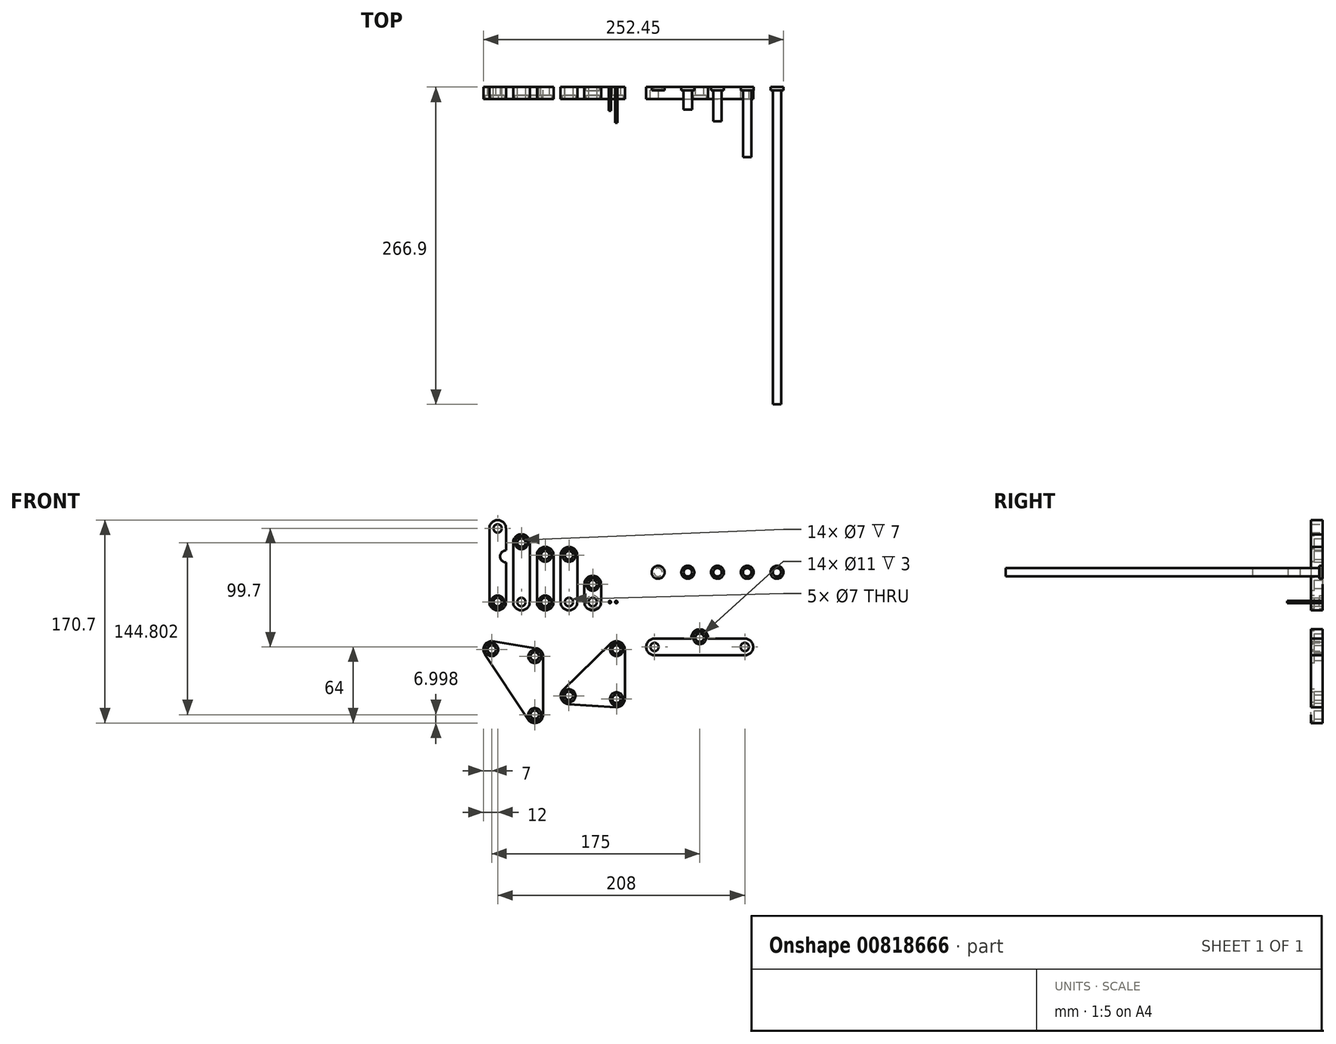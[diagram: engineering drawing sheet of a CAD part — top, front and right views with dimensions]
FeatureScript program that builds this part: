
annotation { "Feature Type Name" : "Feature", "Feature Type Description" : "" }
export const myFeature = defineFeature(function(context is Context, id is Id, definition is map)
    precondition{}
    {
        {
            assignVariable(context, id + "F0", {"name" : "thinkress", "anyValue" : 10});
        }
        {
            var Q0;
            Q0=qCreatedBy(makeId("Front.planeOp"),FACE);
            var sketch = newSketch(context, id + "F1", { "sketchPlane" : qUnion([Q0])});
            skArc(sketch, "E0", {"start": v(-3, 15) * mm, "mid": v(-10, 22) * mm, "end": v(-17, 15) * mm});
            skLineSegment(sketch, "E1", {"start": v(-17, 15) * mm, "end": v(-17, 0) * mm});
            skLineSegment(sketch, "E2", {"start": v(-3, 15) * mm, "end": v(-3, 0) * mm});
            skCircle(sketch, "E3", {"center": v(-10, 15) * mm, "radius": 3.5 * mm});
            skCircle(sketch, "E4", {"center": v(-10, 0) * mm, "radius": 3.5 * mm});
            skArc(sketch, "E5", {"start": v(-37, 0) * mm, "mid": v(-30, -7) * mm, "end": v(-23, 0) * mm});
            skArc(sketch, "E6", {"start": v(-23, 39.3) * mm, "mid": v(-30, 46.3) * mm, "end": v(-37, 39.3) * mm});
            skLineSegment(sketch, "E7", {"start": v(-37, 39.3) * mm, "end": v(-37, 0) * mm});
            skLineSegment(sketch, "E8", {"start": v(-23, 39.3) * mm, "end": v(-23, 0) * mm});
            skCircle(sketch, "E9", {"center": v(-30, 39.3) * mm, "radius": 3.5 * mm});
            skCircle(sketch, "E10", {"center": v(-30, 0) * mm, "radius": 3.5 * mm});
            skArc(sketch, "E11", {"start": v(-57, 0) * mm, "mid": v(-50, -7) * mm, "end": v(-43, 0) * mm});
            skArc(sketch, "E12", {"start": v(-43, 39.4) * mm, "mid": v(-50, 46.4) * mm, "end": v(-57, 39.4) * mm});
            skLineSegment(sketch, "E13", {"start": v(-57, 39.4) * mm, "end": v(-57, 0) * mm});
            skLineSegment(sketch, "E14", {"start": v(-43, 39.4) * mm, "end": v(-43, 0) * mm});
            skCircle(sketch, "E15", {"center": v(-50, 39.4) * mm, "radius": 3.5 * mm});
            skCircle(sketch, "E16", {"center": v(-50, 0) * mm, "radius": 3.5 * mm});
            skArc(sketch, "E17", {"start": v(-77, 0) * mm, "mid": v(-70, -7) * mm, "end": v(-63, 0) * mm});
            skArc(sketch, "E18", {"start": v(-63, 50) * mm, "mid": v(-70, 57) * mm, "end": v(-77, 50) * mm});
            skLineSegment(sketch, "E19", {"start": v(-77, 50) * mm, "end": v(-77, 0) * mm});
            skLineSegment(sketch, "E20", {"start": v(-63, 50) * mm, "end": v(-63, 0) * mm});
            skCircle(sketch, "E21", {"center": v(-70, 50) * mm, "radius": 3.5 * mm});
            skCircle(sketch, "E22", {"center": v(-70, 0) * mm, "radius": 3.5 * mm});
            skArc(sketch, "E23", {"start": v(-97, 0) * mm, "mid": v(-90, -7) * mm, "end": v(-83, 0) * mm});
            skArc(sketch, "E24", {"start": v(-83, 61.9) * mm, "mid": v(-90, 68.9) * mm, "end": v(-97, 61.9) * mm});
            skLineSegment(sketch, "E25", {"start": v(-97, 61.9) * mm, "end": v(-97, 0) * mm});
            skLineSegment(sketch, "E26", {"start": v(-83, 61.9) * mm, "end": v(-83, 0) * mm});
            skCircle(sketch, "E27", {"center": v(-90, 61.9) * mm, "radius": 3.5 * mm});
            skCircle(sketch, "E28", {"center": v(-90, 0) * mm, "radius": 3.5 * mm});
            skLineSegment(sketch, "E29", {"start": v(10, -81.5) * mm, "end": v(10, -40) * mm, "construction": true});
            skLineSegment(sketch, "E30", {"start": v(10, -40) * mm, "end": v(-30.01, -78.9) * mm, "construction": true});
            skLineSegment(sketch, "E31", {"start": v(-30.01, -78.9) * mm, "end": v(10, -81.5) * mm, "construction": true});
            skLineSegment(sketch, "E32", {"start": v(-95, -40) * mm, "end": v(-58.76, -45.8) * mm, "construction": true});
            skPoint(sketch, "E32.startSnap0", {"position": v(-50, -7) * mm});
            skLineSegment(sketch, "E33", {"start": v(-58.76, -45.8) * mm, "end": v(-58.76, -94.8) * mm, "construction": true});
            skLineSegment(sketch, "E34", {"start": v(-58.76, -94.8) * mm, "end": v(-95, -40) * mm, "construction": true});
            skArc(sketch, "E35", {"start": v(17, -40) * mm, "mid": v(12.72, -33.55) * mm, "end": v(5.12, -34.98) * mm});
            skArc(sketch, "E36", {"start": v(9.54, -88.49) * mm, "mid": v(14.79, -86.6) * mm, "end": v(17, -81.5) * mm});
            skArc(sketch, "E37", {"start": v(-34.9, -73.87) * mm, "mid": v(-36.58, -81.31) * mm, "end": v(-30.47, -85.88) * mm});
            skLineSegment(sketch, "E38.0", {"start": v(5.12, -34.98) * mm, "end": v(-34.9, -73.87) * mm});
            skLineSegment(sketch, "E39.0", {"start": v(17, -81.5) * mm, "end": v(17, -40) * mm});
            skLineSegment(sketch, "E40.0", {"start": v(-30.47, -85.88) * mm, "end": v(9.54, -88.49) * mm});
            skCircle(sketch, "E41", {"center": v(-30.01, -78.9) * mm, "radius": 3.5 * mm});
            skCircle(sketch, "E42", {"center": v(10, -40) * mm, "radius": 3.5 * mm});
            skCircle(sketch, "E43", {"center": v(10, -81.5) * mm, "radius": 3.5 * mm});
            skArc(sketch, "E44", {"start": v(-93.9, -33.09) * mm, "mid": v(-100.88, -36.2) * mm, "end": v(-100.84, -43.86) * mm});
            skArc(sketch, "E45", {"start": v(-64.6, -98.66) * mm, "mid": v(-56.75, -101.5) * mm, "end": v(-51.76, -94.8) * mm});
            skArc(sketch, "E46", {"start": v(-51.76, -45.8) * mm, "mid": v(-53.43, -41.26) * mm, "end": v(-57.65, -38.9) * mm});
            skLineSegment(sketch, "E47.0", {"start": v(-64.6, -98.66) * mm, "end": v(-100.84, -43.86) * mm});
            skLineSegment(sketch, "E48.0", {"start": v(-93.9, -33.09) * mm, "end": v(-57.65, -38.9) * mm});
            skLineSegment(sketch, "E49.0", {"start": v(-51.76, -45.8) * mm, "end": v(-51.76, -94.8) * mm});
            skCircle(sketch, "E50", {"center": v(-95, -40) * mm, "radius": 3.5 * mm});
            skCircle(sketch, "E51", {"center": v(-58.76, -45.8) * mm, "radius": 3.5 * mm});
            skCircle(sketch, "E52", {"center": v(-58.76, -94.8) * mm, "radius": 3.5 * mm});
            skLineSegment(sketch, "E53", {"start": v(42, -37.8) * mm, "end": v(80, -37.8) * mm, "construction": true});
            skLineSegment(sketch, "E54", {"start": v(80, -37.8) * mm, "end": v(118, -37.8) * mm, "construction": true});
            skLineSegment(sketch, "E55", {"start": v(80, -37.8) * mm, "end": v(80, -30) * mm, "construction": true});
            skArc(sketch, "E56", {"start": v(42, -30.8) * mm, "mid": v(35, -37.8) * mm, "end": v(42, -44.8) * mm});
            skArc(sketch, "E57", {"start": v(118, -44.8) * mm, "mid": v(125, -37.8) * mm, "end": v(118, -30.8) * mm});
            skArc(sketch, "E58", {"start": v(87, -30) * mm, "mid": v(80, -23) * mm, "end": v(73, -30) * mm});
            skLineSegment(sketch, "E59", {"start": v(42, -44.8) * mm, "end": v(118, -44.8) * mm});
            skLineSegment(sketch, "E60", {"start": v(42, -30.8) * mm, "end": v(73, -30.8) * mm});
            skLineSegment(sketch, "E61", {"start": v(73, -30) * mm, "end": v(73, -30.8) * mm});
            skLineSegment(sketch, "E62", {"start": v(118, -30.8) * mm, "end": v(87, -30.8) * mm});
            skLineSegment(sketch, "E63", {"start": v(87, -30) * mm, "end": v(87, -30.8) * mm});
            skCircle(sketch, "E64", {"center": v(80, -30) * mm, "radius": 3.5 * mm});
            skCircle(sketch, "E65", {"center": v(118, -37.8) * mm, "radius": 3.5 * mm});
            skCircle(sketch, "E66", {"center": v(42, -37.8) * mm, "radius": 3.5 * mm});
            skArc(sketch, "E67", {"start": v(-17, 0) * mm, "mid": v(-10, -7) * mm, "end": v(-3, 0) * mm});
            skSolve(sketch);
        }
        {
            var Q0;
            Q0=makeQuery(id+"F1.imprint","IMPRINT",FACE,{"disambiguationData":[TD([[makeQuery(id+"F1.imprint","IMPRINT",EDGE,{"derivedFrom":sQuery(id+"F1.wireOp",EDGE,"E35")}),1.0]])]});
            var Q1;
            Q1=makeQuery(id+"F1.imprint","IMPRINT",FACE,{"disambiguationData":[TD([[makeQuery(id+"F1.imprint","IMPRINT",EDGE,{"derivedFrom":sQuery(id+"F1.wireOp",EDGE,"E44")}),1.0]])]});
            var Q2;
            Q2=makeQuery(id+"F1.imprint","IMPRINT",FACE,{"disambiguationData":[TD([[makeQuery(id+"F1.imprint","IMPRINT",EDGE,{"derivedFrom":sQuery(id+"F1.wireOp",EDGE,"E23")}),1.0]])]});
            var Q3;
            Q3=makeQuery(id+"F1.imprint","IMPRINT",FACE,{"disambiguationData":[TD([[makeQuery(id+"F1.imprint","IMPRINT",EDGE,{"derivedFrom":sQuery(id+"F1.wireOp",EDGE,"E17")}),1.0]])]});
            var Q4;
            Q4=makeQuery(id+"F1.imprint","IMPRINT",FACE,{"disambiguationData":[TD([[makeQuery(id+"F1.imprint","IMPRINT",EDGE,{"derivedFrom":sQuery(id+"F1.wireOp",EDGE,"E11")}),1.0]])]});
            var Q5;
            Q5=makeQuery(id+"F1.imprint","IMPRINT",FACE,{"disambiguationData":[TD([[makeQuery(id+"F1.imprint","IMPRINT",EDGE,{"derivedFrom":sQuery(id+"F1.wireOp",EDGE,"E5")}),1.0]])]});
            var Q6;
            Q6=makeQuery(id+"F1.imprint","IMPRINT",FACE,{"disambiguationData":[TD([[makeQuery(id+"F1.imprint","IMPRINT",EDGE,{"derivedFrom":sQuery(id+"F1.wireOp",EDGE,"EmJazmCR-fPvo-Zdi6-Hvz8-qesBlYHY8SAY")}),1.0]])]});
            var Q7;
            Q7=makeQuery(id+"F1.imprint","IMPRINT",FACE,{"disambiguationData":[TD([[makeQuery(id+"F1.imprint","IMPRINT",EDGE,{"derivedFrom":sQuery(id+"F1.wireOp",EDGE,"E56")}),1.0]])]});
            var Q8;
            Q8=makeQuery(id+"F1.imprint","IMPRINT",FACE,{"disambiguationData":[TD([[makeQuery(id+"F1.imprint","IMPRINT",EDGE,{"derivedFrom":sQuery(id+"F1.wireOp",EDGE,"E0")}),1.0]])]});
            extrude(context, id + "F2", {"entities" : qUnion([Q0, Q1, Q2, Q3, Q4, Q5, Q6, Q7, Q8]), "depth" : (getVariable(context, 'thinkress')) * mm, "offsetDistance" : 25 * mm});
        }
        {
            var Q0;
            Q0=qCreatedBy(makeId("Front.planeOp"),FACE);
            var sketch = newSketch(context, id + "F3", { "sketchPlane" : qUnion([Q0])});
            skCircle(sketch, "E68", {"center": v(4.4, 0) * mm, "radius": 1 * mm});
            skCircle(sketch, "E69", {"center": v(9.8, 0) * mm, "radius": 1 * mm});
            skSolve(sketch);
        }
        {
            var Q0;
            Q0=makeQuery(id+"F3.imprint","IMPRINT",FACE,{"disambiguationData":[TD([[makeQuery(id+"F3.imprint","IMPRINT",EDGE,{"derivedFrom":sQuery(id+"F3.wireOp",EDGE,"E68")}),1.0]])]});
            extrude(context, id + "F4", {"entities" : qUnion([Q0]), "depth" : (getVariable(context, 'thinkress') * 2) * mm, "offsetDistance" : 25 * mm});
        }
        {
            var Q0;
            Q0=makeQuery(id+"F3.imprint","IMPRINT",FACE,{"disambiguationData":[TD([[makeQuery(id+"F3.imprint","IMPRINT",EDGE,{"derivedFrom":sQuery(id+"F3.wireOp",EDGE,"E69")}),1.0]])]});
            extrude(context, id + "F5", {"entities" : qUnion([Q0]), "depth" : (getVariable(context, 'thinkress') * 3) * mm, "offsetDistance" : 25 * mm});
        }
        {
            var Q0;
            Q0=makeQuery(id+"F2.opExtrude","CAP_FACE",FACE,{"disambiguationData":[OSD([sQuery(id+"F1.wireOp",EDGE,"E23"),sQuery(id+"F1.wireOp",EDGE,"E24"),sQuery(id+"F1.wireOp",EDGE,"E25"),sQuery(id+"F1.wireOp",EDGE,"E26"),sQuery(id+"F1.wireOp",EDGE,"E27"),sQuery(id+"F1.wireOp",EDGE,"E28")])],"isStart":false});
            var sketch = newSketch(context, id + "F6", { "sketchPlane" : qUnion([Q0])});
            skArc(sketch, "E70", {"start": v(-83, 43.4) * mm, "mid": v(-88, 38.4) * mm, "end": v(-83, 33.4) * mm});
            skLineSegment(sketch, "E71.0", {"start": v(-83, 43.4) * mm, "end": v(-83, 33.4) * mm});
            skPoint(sketch, "E72.orphan", {"position": v(-83, 61.9) * mm});
            skPoint(sketch, "E73.orphan", {"position": v(-83, 0) * mm});
            skSolve(sketch);
        }
        {
            var Q0;
            Q0 = qSketchRegion(id + "F6", true);
            extrude(context, id + "F7", {"entities" : qUnion([Q0]), "operationType" : NewBodyOperationType.REMOVE, "endBound" : BoundingType.UP_TO_NEXT, "oppositeDirection" : true, "depth" : 25 * mm, "offsetDistance" : 25 * mm});
        }
        {
            assignVariable(context, id + "F8", {"name" : "nailRoundHigh", "anyValue" : 3});
        }
        {
            assignVariable(context, id + "F9", {"name" : "boardLength", "anyValue" : 110});
        }
        {
            var Q0;
            Q0=makeQuery(id+"F2.opExtrude","CAP_FACE",FACE,{"disambiguationData":[OSD([sQuery(id+"F1.wireOp",EDGE,"E0"),sQuery(id+"F1.wireOp",EDGE,"E1"),sQuery(id+"F1.wireOp",EDGE,"E2"),sQuery(id+"F1.wireOp",EDGE,"E3"),sQuery(id+"F1.wireOp",EDGE,"E4"),sQuery(id+"F1.wireOp",EDGE,"E67")])],"isStart":false});
            var sketch = newSketch(context, id + "F10", { "sketchPlane" : qUnion([Q0])});
            skCircle(sketch, "E74", {"center": v(-10, 15) * mm, "radius": 5.5 * mm});
            skCircle(sketch, "E75", {"center": v(-10, 0) * mm, "radius": 5.5 * mm});
            skSolve(sketch);
        }
        {
            var Q0;
            Q0=makeQuery(id+"F10.imprint","IMPRINT",FACE,{"disambiguationData":[TD([[makeQuery(id+"F10.imprint","IMPRINT",EDGE,{"derivedFrom":sQuery(id+"F10.wireOp",EDGE,"E74")}),1.0]])]});
            extrude(context, id + "F11", {"entities" : qUnion([Q0]), "operationType" : NewBodyOperationType.REMOVE, "oppositeDirection" : true, "depth" : (getVariable(context, 'nailRoundHigh')) * mm, "offsetDistance" : 25 * mm});
        }
        {
            var Q0;
            Q0=makeQuery(id+"F2.opExtrude","CAP_FACE",FACE,{"disambiguationData":[OSD([sQuery(id+"F1.wireOp",EDGE,"E0"),sQuery(id+"F1.wireOp",EDGE,"E1"),sQuery(id+"F1.wireOp",EDGE,"E2"),sQuery(id+"F1.wireOp",EDGE,"E3"),sQuery(id+"F1.wireOp",EDGE,"E4"),sQuery(id+"F1.wireOp",EDGE,"E67")])],"isStart":true});
            var sketch = newSketch(context, id + "F12", { "sketchPlane" : qUnion([Q0])});
            skCircle(sketch, "E76", {"center": v(10, 0) * mm, "radius": 5.5 * mm});
            skSolve(sketch);
        }
        {
            var Q0;
            Q0=makeQuery(id+"F12.imprint","IMPRINT",FACE,{"disambiguationData":[TD([[makeQuery(id+"F12.imprint","IMPRINT",EDGE,{"derivedFrom":sQuery(id+"F12.wireOp",EDGE,"E76")}),1.0]])]});
            extrude(context, id + "F13", {"entities" : qUnion([Q0]), "operationType" : NewBodyOperationType.REMOVE, "oppositeDirection" : true, "depth" : (getVariable(context, 'nailRoundHigh')) * mm, "offsetDistance" : 25 * mm});
        }
        {
            var Q0;
            Q0=makeQuery(id+"F2.opExtrude","CAP_FACE",FACE,{"disambiguationData":[OSD([sQuery(id+"F1.wireOp",EDGE,"E17"),sQuery(id+"F1.wireOp",EDGE,"E18"),sQuery(id+"F1.wireOp",EDGE,"E19"),sQuery(id+"F1.wireOp",EDGE,"E20"),sQuery(id+"F1.wireOp",EDGE,"E21"),sQuery(id+"F1.wireOp",EDGE,"E22")])],"isStart":false});
            var sketch = newSketch(context, id + "F14", { "sketchPlane" : qUnion([Q0])});
            skCircle(sketch, "E77", {"center": v(-70, 50) * mm, "radius": 5.5 * mm});
            skSolve(sketch);
        }
        {
            var Q0;
            Q0=makeQuery(id+"F14.imprint","IMPRINT",FACE,{"disambiguationData":[TD([[makeQuery(id+"F14.imprint","IMPRINT",EDGE,{"derivedFrom":sQuery(id+"F14.wireOp",EDGE,"E77")}),1.0]])]});
            extrude(context, id + "F15", {"entities" : qUnion([Q0]), "operationType" : NewBodyOperationType.REMOVE, "oppositeDirection" : true, "depth" : (getVariable(context, 'nailRoundHigh')) * mm, "offsetDistance" : 25 * mm});
        }
        {
            var Q0;
            Q0=makeQuery(id+"F2.opExtrude","CAP_FACE",FACE,{"disambiguationData":[OSD([sQuery(id+"F1.wireOp",EDGE,"E35"),sQuery(id+"F1.wireOp",EDGE,"E36"),sQuery(id+"F1.wireOp",EDGE,"E37"),sQuery(id+"F1.wireOp",EDGE,"E38.0"),sQuery(id+"F1.wireOp",EDGE,"E39.0"),sQuery(id+"F1.wireOp",EDGE,"E40.0"),sQuery(id+"F1.wireOp",EDGE,"E41"),sQuery(id+"F1.wireOp",EDGE,"E42"),sQuery(id+"F1.wireOp",EDGE,"E43")])],"isStart":false});
            var sketch = newSketch(context, id + "F16", { "sketchPlane" : qUnion([Q0])});
            skCircle(sketch, "E78", {"center": v(10, -40) * mm, "radius": 5.5 * mm});
            skCircle(sketch, "E79", {"center": v(10, -81.5) * mm, "radius": 5.5 * mm});
            skCircle(sketch, "E80", {"center": v(-30.01, -78.9) * mm, "radius": 5.5 * mm});
            skSolve(sketch);
        }
        {
            var Q0;
            Q0 = qSketchRegion(id + "F16", true);
            extrude(context, id + "F17", {"entities" : qUnion([Q0]), "operationType" : NewBodyOperationType.REMOVE, "oppositeDirection" : true, "depth" : (getVariable(context, 'nailRoundHigh')) * mm, "offsetDistance" : 25 * mm});
        }
        {
            var Q0;
            Q0=makeQuery(id+"F2.opExtrude","CAP_FACE",FACE,{"disambiguationData":[OSD([sQuery(id+"F1.wireOp",EDGE,"E44"),sQuery(id+"F1.wireOp",EDGE,"E45"),sQuery(id+"F1.wireOp",EDGE,"E46"),sQuery(id+"F1.wireOp",EDGE,"E47.0"),sQuery(id+"F1.wireOp",EDGE,"E48.0"),sQuery(id+"F1.wireOp",EDGE,"E49.0"),sQuery(id+"F1.wireOp",EDGE,"E50"),sQuery(id+"F1.wireOp",EDGE,"E51"),sQuery(id+"F1.wireOp",EDGE,"E52")])],"isStart":false});
            var sketch = newSketch(context, id + "F18", { "sketchPlane" : qUnion([Q0])});
            skCircle(sketch, "E81", {"center": v(-58.76, -45.8) * mm, "radius": 5.5 * mm});
            skCircle(sketch, "E82", {"center": v(-95, -40) * mm, "radius": 5.5 * mm});
            skCircle(sketch, "E83", {"center": v(-58.76, -94.8) * mm, "radius": 5.5 * mm});
            skSolve(sketch);
        }
        {
            var Q0;
            Q0 = qSketchRegion(id + "F18", true);
            extrude(context, id + "F19", {"entities" : qUnion([Q0]), "operationType" : NewBodyOperationType.REMOVE, "oppositeDirection" : true, "depth" : (getVariable(context, 'nailRoundHigh')) * mm, "offsetDistance" : 25 * mm});
        }
        {
            var Q0;
            Q0=makeQuery(id+"F2.opExtrude","CAP_FACE",FACE,{"disambiguationData":[OSD([sQuery(id+"F1.wireOp",EDGE,"E23"),sQuery(id+"F1.wireOp",EDGE,"E24"),sQuery(id+"F1.wireOp",EDGE,"E25"),sQuery(id+"F1.wireOp",EDGE,"E26"),sQuery(id+"F1.wireOp",EDGE,"E27"),sQuery(id+"F1.wireOp",EDGE,"E28")])],"isStart":false});
            var sketch = newSketch(context, id + "F20", { "sketchPlane" : qUnion([Q0])});
            skCircle(sketch, "E84", {"center": v(-90, 0) * mm, "radius": 5.5 * mm});
            skSolve(sketch);
        }
        {
            var Q0;
            Q0=makeQuery(id+"F20.imprint","IMPRINT",FACE,{"disambiguationData":[TD([[makeQuery(id+"F20.imprint","IMPRINT",EDGE,{"derivedFrom":sQuery(id+"F20.wireOp",EDGE,"E84")}),1.0]])]});
            extrude(context, id + "F21", {"entities" : qUnion([Q0]), "operationType" : NewBodyOperationType.REMOVE, "oppositeDirection" : true, "depth" : (getVariable(context, 'nailRoundHigh')) * mm, "offsetDistance" : 25 * mm});
        }
        {
            var Q0;
            Q0=makeQuery(id+"F2.opExtrude","CAP_FACE",FACE,{"disambiguationData":[OSD([sQuery(id+"F1.wireOp",EDGE,"E11"),sQuery(id+"F1.wireOp",EDGE,"E12"),sQuery(id+"F1.wireOp",EDGE,"E13"),sQuery(id+"F1.wireOp",EDGE,"E14"),sQuery(id+"F1.wireOp",EDGE,"E15"),sQuery(id+"F1.wireOp",EDGE,"E16")])],"isStart":false});
            var sketch = newSketch(context, id + "F22", { "sketchPlane" : qUnion([Q0])});
            skCircle(sketch, "E85", {"center": v(-50, 39.4) * mm, "radius": 5.5 * mm});
            skCircle(sketch, "E86", {"center": v(-50, 0) * mm, "radius": 5.5 * mm});
            skSolve(sketch);
        }
        {
            var Q0;
            Q0 = qSketchRegion(id + "F22", true);
            extrude(context, id + "F23", {"entities" : qUnion([Q0]), "operationType" : NewBodyOperationType.REMOVE, "oppositeDirection" : true, "depth" : (getVariable(context, 'nailRoundHigh')) * mm, "offsetDistance" : 25 * mm});
        }
        {
            var Q0;
            Q0=qCreatedBy(makeId("Front.planeOp"),FACE);
            var sketch = newSketch(context, id + "F24", { "sketchPlane" : qUnion([Q0])});
            skCircle(sketch, "E87", {"center": v(45, 25) * mm, "radius": 5.45 * mm});
            skCircle(sketch, "E88", {"center": v(70, 25) * mm, "radius": 5.45 * mm});
            skCircle(sketch, "E89", {"center": v(95, 25) * mm, "radius": 5.45 * mm});
            skCircle(sketch, "E90", {"center": v(120, 25) * mm, "radius": 5.45 * mm});
            skCircle(sketch, "E91", {"center": v(145, 25) * mm, "radius": 5.45 * mm});
            skSolve(sketch);
        }
        {
            var Q0;
            Q0=makeQuery(id+"F24.imprint","IMPRINT",FACE,{"disambiguationData":[TD([[makeQuery(id+"F24.imprint","IMPRINT",EDGE,{"derivedFrom":sQuery(id+"F24.wireOp",EDGE,"E87")}),1.0]])]});
            var Q1;
            Q1=makeQuery(id+"F24.imprint","IMPRINT",FACE,{"disambiguationData":[TD([[makeQuery(id+"F24.imprint","IMPRINT",EDGE,{"derivedFrom":sQuery(id+"F24.wireOp",EDGE,"E88")}),1.0]])]});
            var Q2;
            Q2=makeQuery(id+"F24.imprint","IMPRINT",FACE,{"disambiguationData":[TD([[makeQuery(id+"F24.imprint","IMPRINT",EDGE,{"derivedFrom":sQuery(id+"F24.wireOp",EDGE,"E89")}),1.0]])]});
            var Q3;
            Q3=makeQuery(id+"F24.imprint","IMPRINT",FACE,{"disambiguationData":[TD([[makeQuery(id+"F24.imprint","IMPRINT",EDGE,{"derivedFrom":sQuery(id+"F24.wireOp",EDGE,"E90")}),1.0]])]});
            var Q4;
            Q4=makeQuery(id+"F24.imprint","IMPRINT",FACE,{"disambiguationData":[TD([[makeQuery(id+"F24.imprint","IMPRINT",EDGE,{"derivedFrom":sQuery(id+"F24.wireOp",EDGE,"E91")}),1.0]])]});
            extrude(context, id + "F25", {"entities" : qUnion([Q0, Q1, Q2, Q3, Q4]), "depth" : (getVariable(context, 'nailRoundHigh') - 0.1) * mm, "offsetDistance" : 25 * mm});
        }
        {
            var Q0;
            Q0=makeQuery(id+"F25.opExtrude","CAP_FACE",FACE,{"disambiguationData":[OSD([sQuery(id+"F24.wireOp",EDGE,"E88")])],"isStart":false});
            var sketch = newSketch(context, id + "F26", { "sketchPlane" : qUnion([Q0])});
            skCircle(sketch, "E92", {"center": v(70, 25) * mm, "radius": 3.5 * mm});
            skCircle(sketch, "E93", {"center": v(95, 25) * mm, "radius": 3.5 * mm});
            skCircle(sketch, "E94", {"center": v(120, 25) * mm, "radius": 3.5 * mm});
            skCircle(sketch, "E95", {"center": v(145, 25) * mm, "radius": 3.5 * mm});
            skSolve(sketch);
        }
        {
            var Q0;
            Q0=makeQuery(id+"F26.imprint","IMPRINT",FACE,{"disambiguationData":[TD([[makeQuery(id+"F26.imprint","IMPRINT",EDGE,{"derivedFrom":sQuery(id+"F26.wireOp",EDGE,"E92")}),1.0]])]});
            extrude(context, id + "F27", {"entities" : qUnion([Q0]), "operationType" : NewBodyOperationType.ADD, "depth" : (2 + getVariable(context, 'thinkress') * 2 - getVariable(context, 'nailRoundHigh') * 2) * mm, "offsetDistance" : 25 * mm});
        }
        {
            var Q0;
            Q0=makeQuery(id+"F26.imprint","IMPRINT",FACE,{"disambiguationData":[TD([[makeQuery(id+"F26.imprint","IMPRINT",EDGE,{"derivedFrom":sQuery(id+"F26.wireOp",EDGE,"E93")}),1.0]])]});
            extrude(context, id + "F28", {"entities" : qUnion([Q0]), "operationType" : NewBodyOperationType.ADD, "depth" : (2 + getVariable(context, 'thinkress') * 3 - getVariable(context, 'nailRoundHigh') * 2) * mm, "offsetDistance" : 25 * mm});
        }
        {
            var Q0;
            Q0=makeQuery(id+"F26.imprint","IMPRINT",FACE,{"disambiguationData":[TD([[makeQuery(id+"F26.imprint","IMPRINT",EDGE,{"derivedFrom":sQuery(id+"F26.wireOp",EDGE,"E94")}),1.0]])]});
            extrude(context, id + "F29", {"entities" : qUnion([Q0]), "operationType" : NewBodyOperationType.ADD, "depth" : (2 + getVariable(context, 'thinkress') * 6 - getVariable(context, 'nailRoundHigh') * 2) * mm, "offsetDistance" : 25 * mm});
        }
        {
            var Q0;
            Q0=makeQuery(id+"F26.imprint","IMPRINT",FACE,{"disambiguationData":[TD([[makeQuery(id+"F26.imprint","IMPRINT",EDGE,{"derivedFrom":sQuery(id+"F26.wireOp",EDGE,"E95")}),1.0]])]});
            extrude(context, id + "F30", {"entities" : qUnion([Q0]), "operationType" : NewBodyOperationType.ADD, "depth" : (getVariable(context, 'boardLength') + getVariable(context, 'thinkress') * 16 - getVariable(context, 'nailRoundHigh') * 2) * mm, "offsetDistance" : 25 * mm});
        }
        {
            var Q0;
            Q0=makeQuery(id+"F2.opExtrude","CAP_FACE",FACE,{"disambiguationData":[OSD([sQuery(id+"F1.wireOp",EDGE,"E5"),sQuery(id+"F1.wireOp",EDGE,"E6"),sQuery(id+"F1.wireOp",EDGE,"E7"),sQuery(id+"F1.wireOp",EDGE,"E8"),sQuery(id+"F1.wireOp",EDGE,"E9"),sQuery(id+"F1.wireOp",EDGE,"E10")])],"isStart":false});
            var sketch = newSketch(context, id + "F31", { "sketchPlane" : qUnion([Q0])});
            skCircle(sketch, "E96", {"center": v(-30, 39.3) * mm, "radius": 5.5 * mm});
            skSolve(sketch);
        }
        {
            var Q0;
            Q0=makeQuery(id+"F31.imprint","IMPRINT",FACE,{"disambiguationData":[TD([[makeQuery(id+"F31.imprint","IMPRINT",EDGE,{"derivedFrom":sQuery(id+"F31.wireOp",EDGE,"E96")}),1.0]])]});
            extrude(context, id + "F32", {"entities" : qUnion([Q0]), "operationType" : NewBodyOperationType.REMOVE, "oppositeDirection" : true, "depth" : (getVariable(context, 'nailRoundHigh')) * mm, "offsetDistance" : 25 * mm});
        }
        {
            var Q0;
            Q0=makeQuery(id+"F2.opExtrude","CAP_FACE",FACE,{"disambiguationData":[OSD([sQuery(id+"F1.wireOp",EDGE,"E56"),sQuery(id+"F1.wireOp",EDGE,"E57"),sQuery(id+"F1.wireOp",EDGE,"E58"),sQuery(id+"F1.wireOp",EDGE,"E59"),sQuery(id+"F1.wireOp",EDGE,"E60"),sQuery(id+"F1.wireOp",EDGE,"E61"),sQuery(id+"F1.wireOp",EDGE,"E62"),sQuery(id+"F1.wireOp",EDGE,"E63"),sQuery(id+"F1.wireOp",EDGE,"E64"),sQuery(id+"F1.wireOp",EDGE,"E65"),sQuery(id+"F1.wireOp",EDGE,"E66")])],"isStart":false});
            var sketch = newSketch(context, id + "F33", { "sketchPlane" : qUnion([Q0])});
            skCircle(sketch, "E97", {"center": v(80, -30) * mm, "radius": 5.5 * mm});
            skSolve(sketch);
        }
        {
            var Q0;
            Q0=makeQuery(id+"F33.imprint","IMPRINT",FACE,{"disambiguationData":[TD([[makeQuery(id+"F33.imprint","IMPRINT",EDGE,{"derivedFrom":sQuery(id+"F33.wireOp",EDGE,"E97")}),1.0]])]});
            extrude(context, id + "F34", {"entities" : qUnion([Q0]), "operationType" : NewBodyOperationType.REMOVE, "oppositeDirection" : true, "depth" : (getVariable(context, 'nailRoundHigh')) * mm, "offsetDistance" : 25 * mm});
        }
        {
            var Q0;
            Q0=makeQuery(id+"F25.opExtrude","CAP_FACE",FACE,{"disambiguationData":[OSD([sQuery(id+"F24.wireOp",EDGE,"E87")])],"isStart":true});
            var sketch = newSketch(context, id + "F35", { "sketchPlane" : qUnion([Q0])});
            skCircle(sketch, "E98", {"center": v(-45, 25) * mm, "radius": 3.5 * mm});
            skSolve(sketch);
        }
        {
            var Q0;
            Q0 = qSketchRegion(id + "F35", true);
            extrude(context, id + "F36", {"entities" : qUnion([Q0]), "operationType" : NewBodyOperationType.REMOVE, "oppositeDirection" : true, "depth" : 2 * mm, "offsetDistance" : 25 * mm});
        }
    });
